# Revit family: Červinka_Přenosný hasicí přístroj_Práškový P2 BETA-L
name_source: partatom
category: Speciální vybavení
units: mm (PartAtom-declared; Revit-internal decimal feet)

## family parameters
Bod výpočtu místnosti = Ne
Kóta kulaté spojky = Použít průměr
Ořezat dutým tvarem při načtení = Ne
Sdílené = Ne
Typ dílu = Normální
Vždy vertikální = Ano
Založené na pracovní rovině = Ano

## types (1)
- P2 BETA-L
    Cena = 0 $
    Hasicí schopnost_ = 13A / 70B / C
    Hasivo = HJ ABC Super Powder
    Hmotnost = 3.75 kg
    Hmotnost hasiva = 2.00 kg
    Komentáře k typům = Přenosný práškový hasicí přístroj
    Kód sestavy = PZ.
    Kód_ = 002BETA
    Materiál hadice = Černá
    Maximální teplota použití = 60 °C
    Minimální teplota použití = -30 °C
    Model = P2 BETA-L
    Objem lahve = 2.45 L
    Popis = Přenosný hasicí přístroj
    Povrchová úprava lahve = Červená
    Pracovní tlak = 14.0 bar
    Průměr lahve = 110 mm  [stored 0.360892 ft]
    Splnění norem = EN3
    Typ zařízení_ = P2 BETA-L
    Třída požáru A = Ano
    Třída požáru B = Ano
    Třída požáru C = Ano
    Třída požáru D = Ne
    Třída požáru F = Ne
    URL = http://www.hasicitechnika.com
    Výchozí výška = 1500 mm  [stored 4.92126 ft]
    Výrobce = ČERVINKA - CZECH REPUBLIC s.r.o.
    Výška k ventilu = 315 mm  [stored 1.03346 ft]
    Výška_ = 395 mm  [stored 1.29593 ft]
    Šířka_ = 150 mm

note: [stored X ft] marks values corroborated as IEEE doubles in the binary element streams (Revit-internal decimal feet)
